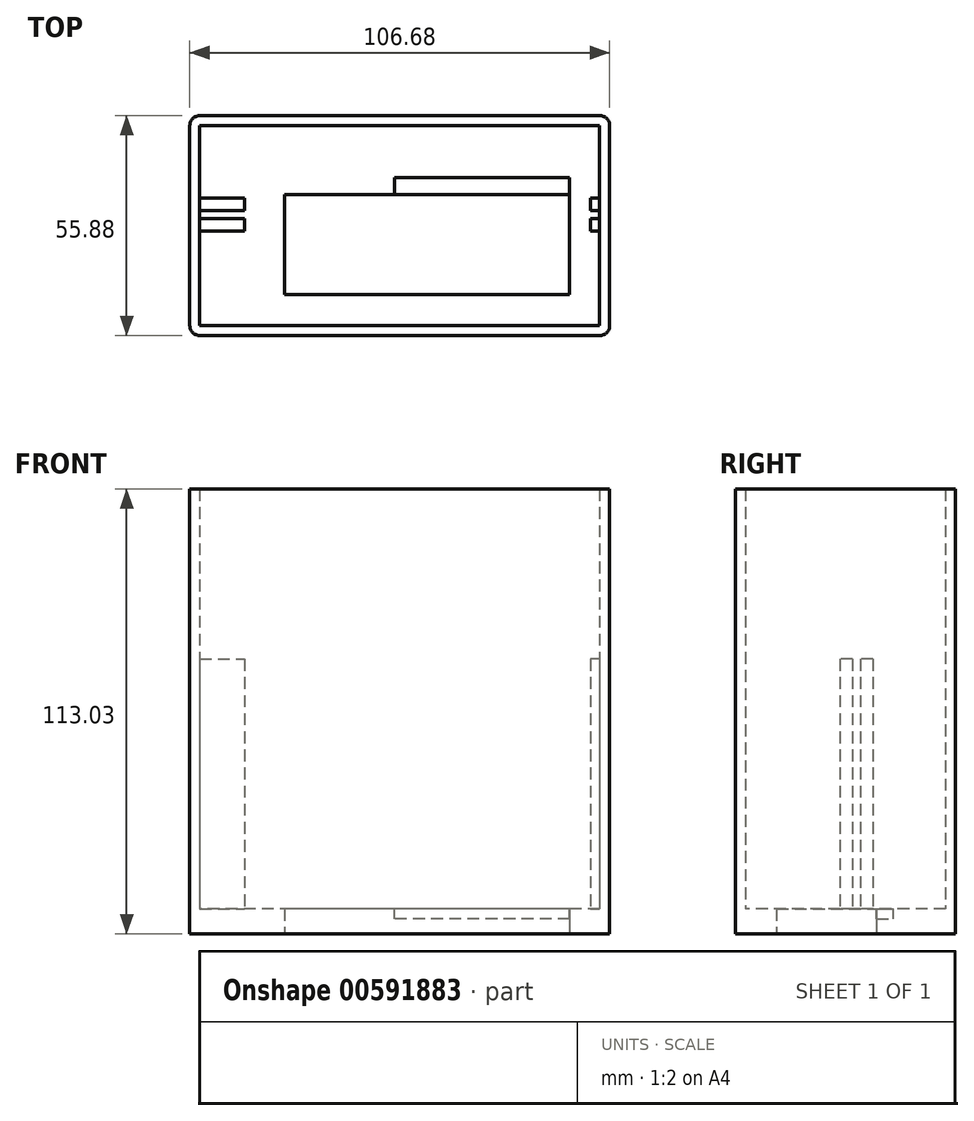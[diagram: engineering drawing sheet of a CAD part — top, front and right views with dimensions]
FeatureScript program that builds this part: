
annotation { "Feature Type Name" : "Feature", "Feature Type Description" : "" }
export const myFeature = defineFeature(function(context is Context, id is Id, definition is map)
    precondition{}
    {
        {
            var Q0;
            Q0=qCreatedBy(makeId("Top.planeOp"),FACE);
            var sketch = newSketch(context, id + "F0", { "sketchPlane" : qUnion([Q0])});
            skLineSegment(sketch, "E0.bottom", {"start": v(50.8, 25.4) * mm, "end": v(-50.8, 25.4) * mm});
            skLineSegment(sketch, "E0.top", {"start": v(50.8, -25.4) * mm, "end": v(-50.8, -25.4) * mm});
            skLineSegment(sketch, "E0.left", {"start": v(50.8, 25.4) * mm, "end": v(50.8, -25.4) * mm});
            skLineSegment(sketch, "E0.right", {"start": v(-50.8, 25.4) * mm, "end": v(-50.8, -25.4) * mm});
            skPoint(sketch, "E0.middle", {"position": v(0, 0) * mm});
            skLineSegment(sketch, "E1.bottom", {"start": v(50.8, 27.94) * mm, "end": v(-50.8, 27.94) * mm});
            skLineSegment(sketch, "E1.top", {"start": v(50.8, -27.94) * mm, "end": v(-50.8, -27.94) * mm});
            skLineSegment(sketch, "E1.left", {"start": v(53.34, 25.4) * mm, "end": v(53.34, -25.4) * mm});
            skLineSegment(sketch, "E1.right", {"start": v(-53.34, 25.4) * mm, "end": v(-53.34, -25.4) * mm});
            skLineSegment(sketch, "E2.bottom", {"start": v(43.18, -17.53) * mm, "end": v(-29.21, -17.53) * mm});
            skLineSegment(sketch, "E2.top", {"start": v(43.18, 7.87) * mm, "end": v(-29.21, 7.87) * mm});
            skLineSegment(sketch, "E2.left", {"start": v(43.18, -17.53) * mm, "end": v(43.18, 7.87) * mm});
            skLineSegment(sketch, "E2.right", {"start": v(-29.21, -17.53) * mm, "end": v(-29.21, 7.87) * mm});
            skPoint(sketch, "E2.middle", {"position": v(-3.81, 0) * mm});
            skPoint(sketch, "E3.visualSharp", {"position": v(53.34, 27.94) * mm});
            skArc(sketch, "E3.filletArc", {"start": v(53.34, 25.4) * mm, "mid": v(52.6, 27.2) * mm, "end": v(50.8, 27.94) * mm});
            skPoint(sketch, "E4.visualSharp", {"position": v(-53.34, 27.94) * mm});
            skArc(sketch, "E4.filletArc", {"start": v(-50.8, 27.94) * mm, "mid": v(-52.6, 27.2) * mm, "end": v(-53.34, 25.4) * mm});
            skPoint(sketch, "E5.visualSharp", {"position": v(-53.34, -27.94) * mm});
            skArc(sketch, "E5.filletArc", {"start": v(-53.34, -25.4) * mm, "mid": v(-52.6, -27.2) * mm, "end": v(-50.8, -27.94) * mm});
            skPoint(sketch, "E6.visualSharp", {"position": v(53.34, -27.94) * mm});
            skArc(sketch, "E6.filletArc", {"start": v(50.8, -27.94) * mm, "mid": v(52.6, -27.2) * mm, "end": v(53.34, -25.4) * mm});
            skSolve(sketch);
        }
        {
            var Q0;
            Q0=makeQuery(id+"F0.imprint","IMPRINT",FACE,{"disambiguationData":[TD([[makeQuery(id+"F0.imprint","IMPRINT",EDGE,{"derivedFrom":sQuery(id+"F0.wireOp",EDGE,"E0.bottom")}),-1.0]])]});
            extrude(context, id + "F1", {"entities" : qUnion([Q0]), "depth" : 113.03 * mm, "offsetDistance" : 25.4 * mm});
        }
        {
            var Q0;
            Q0 = qSketchRegion(id + "F0", true);
            var Q1;
            Q1=makeQuery(id+"F0.imprint","IMPRINT",FACE,{"disambiguationData":[TD([[makeQuery(id+"F0.imprint","IMPRINT",EDGE,{"derivedFrom":sQuery(id+"F0.wireOp",EDGE,"E0.bottom")}),1.0]])]});
            extrude(context, id + "F2", {"entities" : qUnion([Q0, Q1]), "operationType" : NewBodyOperationType.ADD, "depth" : 6.35 * mm, "offsetDistance" : 25.4 * mm});
        }
        {
            var Q0;
            Q0=makeQuery(id+"F2.opExtrude","CAP_FACE",FACE,{"disambiguationData":[OSD([sQuery(id+"F0.wireOp",EDGE,"E1.bottom"),sQuery(id+"F0.wireOp",EDGE,"E1.top"),sQuery(id+"F0.wireOp",EDGE,"E1.left"),sQuery(id+"F0.wireOp",EDGE,"E1.right"),sQuery(id+"F0.wireOp",EDGE,"E2.bottom"),sQuery(id+"F0.wireOp",EDGE,"E2.top"),sQuery(id+"F0.wireOp",EDGE,"E2.left"),sQuery(id+"F0.wireOp",EDGE,"E2.right")])],"isStart":false});
            var sketch = newSketch(context, id + "F3", { "sketchPlane" : qUnion([Q0])});
            skLineSegment(sketch, "E7.bottom", {"start": v(43.18, 7.87) * mm, "end": v(-1.27, 7.87) * mm});
            skLineSegment(sketch, "E7.top", {"start": v(43.18, 12.2) * mm, "end": v(-1.27, 12.2) * mm});
            skLineSegment(sketch, "E7.left", {"start": v(43.18, 7.87) * mm, "end": v(43.18, 12.2) * mm});
            skLineSegment(sketch, "E7.right", {"start": v(-1.27, 7.87) * mm, "end": v(-1.27, 12.2) * mm});
            skSolve(sketch);
        }
        {
            var Q0;
            Q0 = qSketchRegion(id + "F3", true);
            extrude(context, id + "F4", {"entities" : qUnion([Q0]), "operationType" : NewBodyOperationType.REMOVE, "oppositeDirection" : true, "depth" : 2.54 * mm, "offsetDistance" : 25.4 * mm});
        }
        {
            var Q0;
            Q0=makeQuery(id+"F2.opExtrude","CAP_FACE",FACE,{"disambiguationData":[OSD([sQuery(id+"F0.wireOp",EDGE,"E1.bottom"),sQuery(id+"F0.wireOp",EDGE,"E1.top"),sQuery(id+"F0.wireOp",EDGE,"E1.left"),sQuery(id+"F0.wireOp",EDGE,"E1.right"),sQuery(id+"F0.wireOp",EDGE,"E2.bottom"),sQuery(id+"F0.wireOp",EDGE,"E2.top"),sQuery(id+"F0.wireOp",EDGE,"E2.left"),sQuery(id+"F0.wireOp",EDGE,"E2.right"),sQuery(id+"F0.wireOp",EDGE,"E3.filletArc"),sQuery(id+"F0.wireOp",EDGE,"E4.filletArc"),sQuery(id+"F0.wireOp",EDGE,"E5.filletArc"),sQuery(id+"F0.wireOp",EDGE,"E6.filletArc")])],"isStart":false});
            var sketch = newSketch(context, id + "F5", { "sketchPlane" : qUnion([Q0])});
            skLineSegment(sketch, "E8", {"start": v(-50.8, 6.98) * mm, "end": v(-39.37, 6.99) * mm});
            skLineSegment(sketch, "E9", {"start": v(-39.37, 6.99) * mm, "end": v(-39.37, 3.81) * mm});
            skLineSegment(sketch, "E10", {"start": v(-39.37, 3.81) * mm, "end": v(-50.8, 3.8) * mm});
            skLineSegment(sketch, "E11", {"start": v(-50.8, 1.78) * mm, "end": v(-39.37, 1.78) * mm});
            skLineSegment(sketch, "E12", {"start": v(-39.37, 1.78) * mm, "end": v(-39.37, -1.4) * mm});
            skLineSegment(sketch, "E13", {"start": v(-39.37, -1.4) * mm, "end": v(-50.8, -1.4) * mm});
            skSolve(sketch);
        }
        {
            var Q0;
            Q0 = qSketchRegion(id + "F5", true);
            var Q1;
            {var subQ0=sQuery(id+"F5.wireOp",EDGE,"E8");Q1=makeQuery(id+"F5.imprint","IMPRINT",FACE,{"disambiguationData":[TD([[makeQuery(id+"F5.imprint","IMPRINT",EDGE,{"derivedFrom":subQ0}),-1.0]])]});}
            var Q2;
            {var subQ0=sQuery(id+"F5.wireOp",EDGE,"E11");Q2=makeQuery(id+"F5.imprint","IMPRINT",FACE,{"disambiguationData":[TD([[makeQuery(id+"F5.imprint","IMPRINT",EDGE,{"derivedFrom":subQ0}),-1.0]])]});}
            extrude(context, id + "F6", {"entities" : qUnion([Q0, Q1, Q2]), "operationType" : NewBodyOperationType.ADD, "depth" : 63.5 * mm, "offsetDistance" : 25.4 * mm});
        }
        {
            var Q0;
            Q0=makeQuery(id+"F2.opExtrude","CAP_FACE",FACE,{"disambiguationData":[OSD([sQuery(id+"F0.wireOp",EDGE,"E1.bottom"),sQuery(id+"F0.wireOp",EDGE,"E1.top"),sQuery(id+"F0.wireOp",EDGE,"E1.left"),sQuery(id+"F0.wireOp",EDGE,"E1.right"),sQuery(id+"F0.wireOp",EDGE,"E2.bottom"),sQuery(id+"F0.wireOp",EDGE,"E2.top"),sQuery(id+"F0.wireOp",EDGE,"E2.left"),sQuery(id+"F0.wireOp",EDGE,"E2.right"),sQuery(id+"F0.wireOp",EDGE,"E3.filletArc"),sQuery(id+"F0.wireOp",EDGE,"E4.filletArc"),sQuery(id+"F0.wireOp",EDGE,"E5.filletArc"),sQuery(id+"F0.wireOp",EDGE,"E6.filletArc")])],"isStart":false});
            var sketch = newSketch(context, id + "F7", { "sketchPlane" : qUnion([Q0])});
            skLineSegment(sketch, "E14", {"start": v(50.8, 6.99) * mm, "end": v(48.51, 6.99) * mm});
            skLineSegment(sketch, "E15", {"start": v(48.51, 6.99) * mm, "end": v(48.51, 3.81) * mm});
            skLineSegment(sketch, "E16", {"start": v(48.51, 3.81) * mm, "end": v(50.8, 3.81) * mm});
            skLineSegment(sketch, "E17", {"start": v(50.8, 1.78) * mm, "end": v(48.51, 1.78) * mm});
            skLineSegment(sketch, "E18", {"start": v(48.51, 1.78) * mm, "end": v(48.51, -1.4) * mm});
            skLineSegment(sketch, "E19", {"start": v(48.51, -1.4) * mm, "end": v(50.8, -1.4) * mm});
            skSolve(sketch);
        }
        {
            var Q0;
            Q0 = qSketchRegion(id + "F7", true);
            var Q1;
            {var subQ0=sQuery(id+"F7.wireOp",EDGE,"E14");Q1=makeQuery(id+"F7.imprint","IMPRINT",FACE,{"disambiguationData":[TD([[makeQuery(id+"F7.imprint","IMPRINT",EDGE,{"derivedFrom":subQ0}),1.0]])]});}
            var Q2;
            {var subQ0=sQuery(id+"F7.wireOp",EDGE,"E17");Q2=makeQuery(id+"F7.imprint","IMPRINT",FACE,{"disambiguationData":[TD([[makeQuery(id+"F7.imprint","IMPRINT",EDGE,{"derivedFrom":subQ0}),1.0]])]});}
            extrude(context, id + "F8", {"entities" : qUnion([Q0, Q1, Q2]), "operationType" : NewBodyOperationType.ADD, "depth" : 63.5 * mm, "offsetDistance" : 25.4 * mm});
        }
    });
